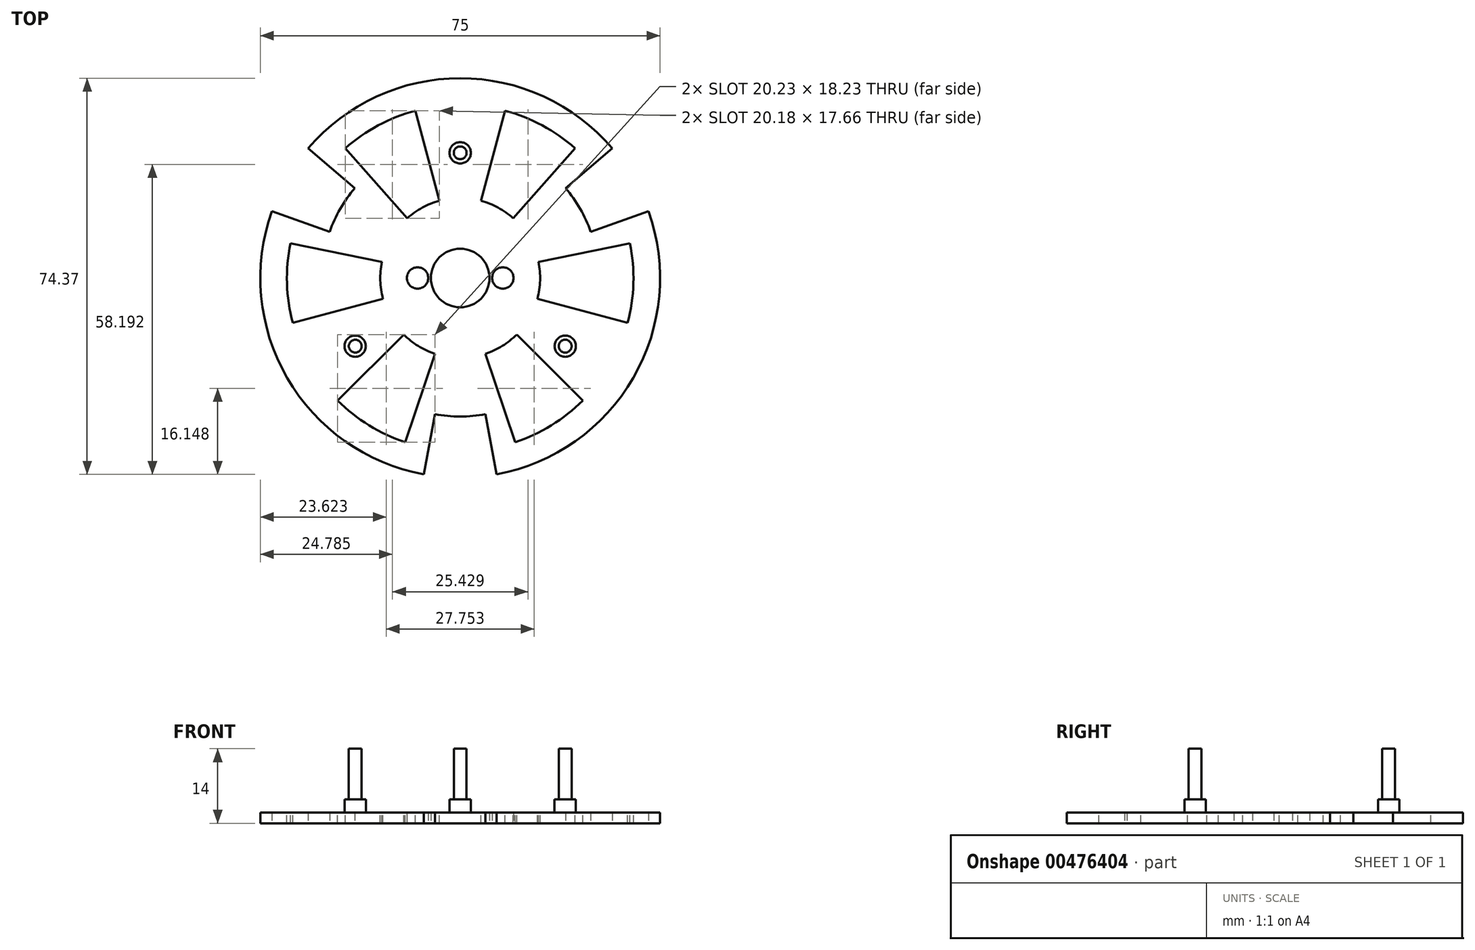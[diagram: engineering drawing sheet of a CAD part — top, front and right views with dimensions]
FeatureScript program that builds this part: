
annotation { "Feature Type Name" : "Feature", "Feature Type Description" : "" }
export const myFeature = defineFeature(function(context is Context, id is Id, definition is map)
    precondition{}
    {
        {
            var Q0;
            Q0=qCreatedBy(makeId("Top.planeOp"),FACE);
            var sketch = newSketch(context, id + "F0", { "sketchPlane" : qUnion([Q0])});
            skArc(sketch, "E0", {"start": v(6.83, -36.87) * mm, "mid": v(32.48, -18.75) * mm, "end": v(35.35, 12.52) * mm});
            skCircle(sketch, "E1", {"center": v(0, 0) * mm, "radius": 5.5 * mm});
            skLineSegment(sketch, "E2", {"start": v(0, 0) * mm, "end": v(-4.74, -25.56) * mm, "construction": true});
            skLineSegment(sketch, "E3", {"start": v(-4.74, -25.56) * mm, "end": v(-4.74, -25.56) * mm});
            skLineSegment(sketch, "E4", {"start": v(0, 0) * mm, "end": v(4.74, -25.56) * mm, "construction": true});
            skLineSegment(sketch, "E5", {"start": v(4.74, -25.56) * mm, "end": v(6.83, -36.87) * mm});
            skLineSegment(sketch, "E6", {"start": v(0, 0) * mm, "end": v(0, -37.5) * mm, "construction": true});
            skArc(sketch, "E7", {"start": v(-4.74, -25.56) * mm, "mid": v(0, -26) * mm, "end": v(4.74, -25.56) * mm});
            skLineSegment(sketch, "E8", {"start": v(-6.83, -36.87) * mm, "end": v(-4.74, -25.56) * mm});
            skLineSegment(sketch, "E9", {"start": v(-4.74, -25.56) * mm, "end": v(-6.83, -36.87) * mm, "construction": true});
            skLineSegment(sketch, "E10.1.0", {"start": v(35.35, 12.52) * mm, "end": v(24.5, 8.68) * mm});
            skLineSegment(sketch, "E10.1.1", {"start": v(24.5, 8.68) * mm, "end": v(24.5, 8.68) * mm});
            skLineSegment(sketch, "E10.1.2", {"start": v(24.5, 8.68) * mm, "end": v(24.5, 8.68) * mm});
            skArc(sketch, "E10.1.3", {"start": v(24.5, 8.68) * mm, "mid": v(22.52, 13) * mm, "end": v(19.77, 16.89) * mm});
            skLineSegment(sketch, "E10.1.4", {"start": v(19.77, 16.89) * mm, "end": v(28.52, 24.35) * mm});
            skLineSegment(sketch, "E10.2.0", {"start": v(-28.52, 24.35) * mm, "end": v(-19.77, 16.89) * mm});
            skLineSegment(sketch, "E10.2.1", {"start": v(-19.77, 16.89) * mm, "end": v(-19.77, 16.89) * mm});
            skLineSegment(sketch, "E10.2.2", {"start": v(-19.77, 16.89) * mm, "end": v(-19.77, 16.89) * mm});
            skArc(sketch, "E10.2.3", {"start": v(-19.77, 16.89) * mm, "mid": v(-22.52, 13) * mm, "end": v(-24.5, 8.68) * mm});
            skLineSegment(sketch, "E10.2.4", {"start": v(-24.5, 8.68) * mm, "end": v(-35.35, 12.52) * mm});
            skArc(sketch, "E11.trimOffspring", {"start": v(-35.35, 12.52) * mm, "mid": v(-32.48, -18.75) * mm, "end": v(-6.83, -36.87) * mm});
            skArc(sketch, "E12.trimOffspring", {"start": v(28.52, 24.35) * mm, "mid": v(0, 37.5) * mm, "end": v(-28.52, 24.35) * mm});
            skLineSegment(sketch, "E13", {"start": v(-6.83, -36.87) * mm, "end": v(0, -37.5) * mm, "construction": true});
            skLineSegment(sketch, "E14", {"start": v(6.83, -36.87) * mm, "end": v(0, -37.5) * mm, "construction": true});
            skCircle(sketch, "E15", {"center": v(-8, 0) * mm, "radius": 2 * mm});
            skLineSegment(sketch, "E16", {"start": v(0, 0) * mm, "end": v(-8, 0) * mm, "construction": true});
            skCircle(sketch, "E17.0.MirrorC", {"center": v(8, 0) * mm, "radius": 2 * mm});
            skSolve(sketch);
        }
        {
            var Q0;
            Q0=qSketchRegion(id+"F0",true);
            extrude(context, id + "F1", {"entities" : qUnion([Q0]), "depth" : 2 * mm});
        }
        {
            var Q0;
            Q0=makeQuery(id+"F1.opExtrude","CAP_FACE",FACE,{"disambiguationData":[OSD([sQuery(id+"F0.wireOp",EDGE,"E0"),sQuery(id+"F0.wireOp",EDGE,"E1"),sQuery(id+"F0.wireOp",EDGE,"E5"),sQuery(id+"F0.wireOp",EDGE,"E7"),sQuery(id+"F0.wireOp",EDGE,"E8"),sQuery(id+"F0.wireOp",EDGE,"E3"),sQuery(id+"F0.wireOp",EDGE,"E10.1.0"),sQuery(id+"F0.wireOp",EDGE,"E10.1.1"),sQuery(id+"F0.wireOp",EDGE,"E10.1.3"),sQuery(id+"F0.wireOp",EDGE,"E10.1.4"),sQuery(id+"F0.wireOp",EDGE,"E10.2.0"),sQuery(id+"F0.wireOp",EDGE,"E10.2.1"),sQuery(id+"F0.wireOp",EDGE,"E10.2.3"),sQuery(id+"F0.wireOp",EDGE,"E10.2.4"),sQuery(id+"F0.wireOp",EDGE,"E11.trimOffspring"),sQuery(id+"F0.wireOp",EDGE,"E12.trimOffspring")])],"isStart":false});
            var sketch = newSketch(context, id + "F2", { "sketchPlane" : qUnion([Q0])});
            skCircle(sketch, "E18", {"center": v(0, 23.5) * mm, "radius": 2 * mm});
            skCircle(sketch, "E19.1.0", {"center": v(-19.7, -12.8) * mm, "radius": 2 * mm});
            skCircle(sketch, "E19.2.0", {"center": v(19.7, -12.8) * mm, "radius": 2 * mm});
            skPoint(sketch, "E19.center", {"position": v(0, 0) * mm});
            skLineSegment(sketch, "E20", {"start": v(0, 0) * mm, "end": v(0, 23.5) * mm, "construction": true});
            skLineSegment(sketch, "E21", {"start": v(0, 0) * mm, "end": v(19.7, -12.8) * mm, "construction": true});
            skLineSegment(sketch, "E22", {"start": v(0, 0) * mm, "end": v(-19.7, -12.8) * mm, "construction": true});
            skSolve(sketch);
        }
        {
            var Q0;
            Q0=qSketchRegion(id+"F2",true);
            extrude(context, id + "F3", {"entities" : qUnion([Q0]), "operationType" : NewBodyOperationType.ADD, "depth" : 2.5 * mm});
        }
        {
            var Q0;
            Q0=makeQuery(id+"F3.opExtrude","CAP_FACE",FACE,{"disambiguationData":[OSD([sQuery(id+"F2.wireOp",EDGE,"E18")])],"isStart":false});
            var sketch = newSketch(context, id + "F4", { "sketchPlane" : qUnion([Q0])});
            skCircle(sketch, "E23", {"center": v(0, 23.5) * mm, "radius": 1.2 * mm});
            skCircle(sketch, "E24.1.0", {"center": v(-19.7, -12.8) * mm, "radius": 1.2 * mm});
            skCircle(sketch, "E24.2.0", {"center": v(19.7, -12.8) * mm, "radius": 1.2 * mm});
            skPoint(sketch, "E24.center", {"position": v(0, 0) * mm});
            skSolve(sketch);
        }
        {
            var Q0;
            Q0=qSketchRegion(id+"F4",true);
            extrude(context, id + "F5", {"entities" : qUnion([Q0]), "operationType" : NewBodyOperationType.ADD, "depth" : 9.5 * mm});
        }
        {
            var Q0;
            Q0=makeQuery(id+"F1.opExtrude","CAP_FACE",FACE,{"disambiguationData":[OSD([sQuery(id+"F0.wireOp",EDGE,"E0"),sQuery(id+"F0.wireOp",EDGE,"E1"),sQuery(id+"F0.wireOp",EDGE,"E5"),sQuery(id+"F0.wireOp",EDGE,"E7"),sQuery(id+"F0.wireOp",EDGE,"E8"),sQuery(id+"F0.wireOp",EDGE,"E10.1.0"),sQuery(id+"F0.wireOp",EDGE,"E10.1.3"),sQuery(id+"F0.wireOp",EDGE,"E10.1.4"),sQuery(id+"F0.wireOp",EDGE,"E10.2.0"),sQuery(id+"F0.wireOp",EDGE,"E10.2.3"),sQuery(id+"F0.wireOp",EDGE,"E10.2.4"),sQuery(id+"F0.wireOp",EDGE,"E11.trimOffspring"),sQuery(id+"F0.wireOp",EDGE,"E12.trimOffspring"),sQuery(id+"F0.wireOp",EDGE,"E15"),sQuery(id+"F0.wireOp",EDGE,"E17.0.MirrorC")])],"isStart":false});
            var sketch = newSketch(context, id + "F6", { "sketchPlane" : qUnion([Q0])});
            skLineSegment(sketch, "E25", {"start": v(0, 0) * mm, "end": v(9.94, 11.23) * mm, "construction": true});
            skLineSegment(sketch, "E26", {"start": v(9.94, 11.23) * mm, "end": v(21.55, 24.35) * mm});
            skLineSegment(sketch, "E27", {"start": v(0, 0) * mm, "end": v(3.88, 14.49) * mm, "construction": true});
            skLineSegment(sketch, "E28", {"start": v(3.88, 14.49) * mm, "end": v(8.42, 31.4) * mm});
            skArc(sketch, "E29", {"start": v(21.55, 24.35) * mm, "mid": v(15.4, 28.64) * mm, "end": v(8.42, 31.4) * mm});
            skArc(sketch, "E30", {"start": v(9.94, 11.23) * mm, "mid": v(7.1, 13.21) * mm, "end": v(3.88, 14.49) * mm});
            skLineSegment(sketch, "E31", {"start": v(0, 0) * mm, "end": v(-3.88, 14.49) * mm, "construction": true});
            skLineSegment(sketch, "E32", {"start": v(-3.88, 14.49) * mm, "end": v(-8.42, 31.4) * mm});
            skLineSegment(sketch, "E33", {"start": v(0, 0) * mm, "end": v(-9.94, 11.23) * mm, "construction": true});
            skLineSegment(sketch, "E34", {"start": v(-9.94, 11.23) * mm, "end": v(-21.55, 24.35) * mm});
            skArc(sketch, "E35", {"start": v(-8.42, 31.4) * mm, "mid": v(-15.4, 28.64) * mm, "end": v(-21.55, 24.35) * mm});
            skArc(sketch, "E36", {"start": v(-3.88, 14.49) * mm, "mid": v(-7.1, 13.21) * mm, "end": v(-9.94, 11.23) * mm});
            skLineSegment(sketch, "E37", {"start": v(-8.42, 31.4) * mm, "end": v(0, 31.4) * mm, "construction": true});
            skLineSegment(sketch, "E38", {"start": v(0, 31.4) * mm, "end": v(8.42, 31.4) * mm, "construction": true});
            skLineSegment(sketch, "E39", {"start": v(-28.52, 24.35) * mm, "end": v(-21.55, 24.35) * mm, "construction": true});
            skLineSegment(sketch, "E40", {"start": v(21.55, 24.35) * mm, "end": v(28.52, 24.35) * mm, "construction": true});
            skArc(sketch, "E41.1.0", {"start": v(-10.6, -10.6) * mm, "mid": v(-7.9, -12.76) * mm, "end": v(-4.76, -14.22) * mm});
            skArc(sketch, "E41.1.1", {"start": v(-14.7, 3) * mm, "mid": v(-15, -0.46) * mm, "end": v(-14.49, -3.88) * mm});
            skLineSegment(sketch, "E41.1.2", {"start": v(-14.49, -3.88) * mm, "end": v(-31.4, -8.42) * mm});
            skLineSegment(sketch, "E41.1.3", {"start": v(-10.6, -10.6) * mm, "end": v(-23, -23) * mm});
            skLineSegment(sketch, "E41.1.4", {"start": v(-4.76, -14.22) * mm, "end": v(-10.32, -30.84) * mm});
            skLineSegment(sketch, "E41.1.5", {"start": v(-14.7, 3) * mm, "end": v(-31.86, 6.48) * mm});
            skArc(sketch, "E41.1.6", {"start": v(-23, -23) * mm, "mid": v(-17.11, -27.65) * mm, "end": v(-10.32, -30.84) * mm});
            skArc(sketch, "E41.1.7", {"start": v(-31.86, 6.48) * mm, "mid": v(-32.5, -1) * mm, "end": v(-31.4, -8.42) * mm});
            skArc(sketch, "E41.2.0", {"start": v(14.49, -3.88) * mm, "mid": v(15, -0.46) * mm, "end": v(14.7, 3) * mm});
            skArc(sketch, "E41.2.1", {"start": v(4.76, -14.22) * mm, "mid": v(7.9, -12.76) * mm, "end": v(10.6, -10.6) * mm});
            skLineSegment(sketch, "E41.2.2", {"start": v(10.6, -10.6) * mm, "end": v(23, -23) * mm});
            skLineSegment(sketch, "E41.2.3", {"start": v(14.49, -3.88) * mm, "end": v(31.4, -8.42) * mm});
            skLineSegment(sketch, "E41.2.4", {"start": v(14.7, 3) * mm, "end": v(31.86, 6.48) * mm});
            skLineSegment(sketch, "E41.2.5", {"start": v(4.76, -14.22) * mm, "end": v(10.32, -30.84) * mm});
            skArc(sketch, "E41.2.6", {"start": v(31.4, -8.42) * mm, "mid": v(32.5, -1) * mm, "end": v(31.86, 6.48) * mm});
            skArc(sketch, "E41.2.7", {"start": v(10.32, -30.84) * mm, "mid": v(17.11, -27.65) * mm, "end": v(23, -23) * mm});
            skSolve(sketch);
        }
        {
            var Q0;
            Q0=qSketchRegion(id+"F6",true);
            extrude(context, id + "F7", {"entities" : qUnion([Q0]), "operationType" : NewBodyOperationType.REMOVE, "endBound" : BoundingType.UP_TO_NEXT, "oppositeDirection" : true, "depth" : 25 * mm});
        }
    });
